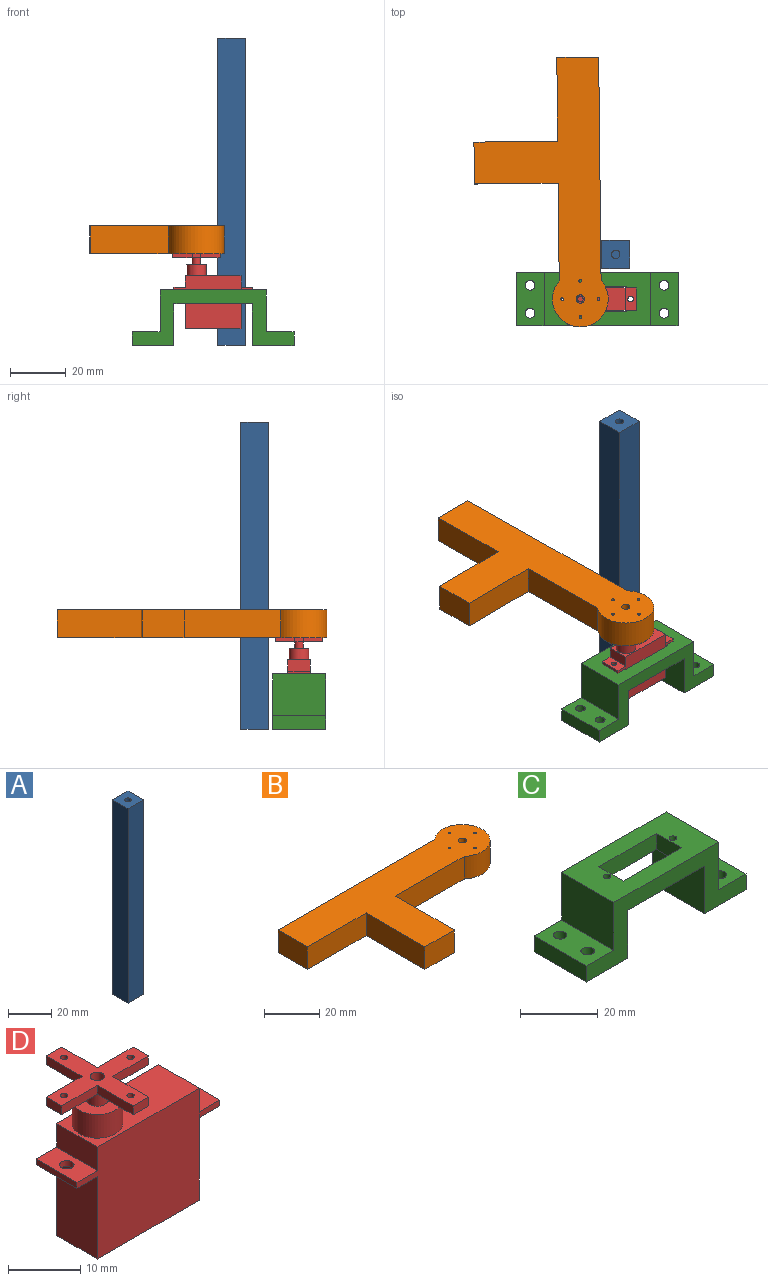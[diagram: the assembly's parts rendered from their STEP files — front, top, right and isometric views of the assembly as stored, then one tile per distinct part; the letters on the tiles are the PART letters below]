
ASSEMBLY  parts=4 mates=2
PART A: 10 faces, bbox 10x10x110 mm
  f0: plane 110x10mm, normal (1,0,0), area 1100mm2, adj f1,f3,f4,f5
  f1: plane 110x10mm, normal (0,1,0), area 1100mm2, adj f0,f2,f4,f5
  f2: plane 110x10mm, normal (-1,0,0), area 1100mm2, adj f1,f3,f4,f5
  f3: plane 110x10mm, normal (0,-1,0), area 1100mm2, adj f0,f2,f4,f5
  f4: plane 10x10mm, normal (0,0,1), area 92.9mm2, adj f0,f1,f2,f3,f8
  f5: plane 10x10mm, normal (0,0,-1), area 92.9mm2, adj f0,f1,f2,f3,f6
  f6: cylinder r=1.5mm len=20mm, axis (0,0,-1), area 188.5mm2, adj f5,f7
  f7: plane 3x3mm, normal (0,0,-1), area 7.1mm2, adj f6
  f8: cylinder r=1.5mm len=30mm, axis (0,0,1), area 282.7mm2, adj f4,f9
  f9: plane 3x3mm, normal (0,0,1), area 7.1mm2, adj f8
PART B: 15 faces, bbox 96.6x47.5x10 mm
  f0: cylinder r=10mm len=20mm, axis (0,0,-1), area 458.7mm2, adj f1,f12,f13,f14
  f1: plane 80x10mm, normal (0,1,0), area 800mm2, adj f0,f2,f13,f14
  f2: plane 15x10mm, normal (-1,0,0), area 150mm2, adj f1,f3,f13,f14
  f3: plane 30x10mm, normal (0,-1,0), area 300mm2, adj f2,f4,f13,f14
  f4: plane 30x10mm, normal (-1,0,0), area 300mm2, adj f3,f5,f13,f14
  f5: plane 15x10mm, normal (0,-1,0), area 150mm2, adj f4,f6,f13,f14
  f6: plane 30x10mm, normal (1,0,0), area 300mm2, adj f5,f12,f13,f14
  f7: cylinder r=1.5mm len=10mm, axis (0,0,-1), area 94.2mm2, adj f13,f14
  f8: cylinder r=0.5mm len=10mm, axis (0,0,-1), area 31.4mm2, adj f13,f14
  f9: cylinder r=0.5mm len=10mm, axis (0,0,-1), area 31.4mm2, adj f13,f14
  f10: cylinder r=0.5mm len=10mm, axis (0,0,-1), area 31.4mm2, adj f13,f14
  f11: cylinder r=0.5mm len=10mm, axis (0,0,-1), area 31.4mm2, adj f13,f14
  f12: plane 35x10mm, normal (0,-1,0), area 350mm2, adj f0,f6,f13,f14
  f13: plane 96.61x47.5mm, normal (0,0,1), area 1918.8mm2, adj f0,f1,f2,f3,f4,f5,f6,f7
  f14: plane 96.61x47.5mm, normal (0,0,-1), area 1918.8mm2, adj f0,f1,f2,f3,f4,f5,f6,f7
PART C: 24 faces, bbox 58x19x20 mm
  f0: plane 28x19mm, normal (0,0,-1), area 336.7mm2, adj f6,f7,f12,f13,f14,f15,f16,f17
  f1: plane 38x19mm, normal (0,0,1), area 526.7mm2, adj f2,f11,f12,f13,f14,f15,f16,f17
  f2: plane 19x15mm, normal (-1,0,0), area 285mm2, adj f1,f3,f12,f13
  f3: plane 19x10mm, normal (0,0,1), area 170.8mm2, adj f2,f4,f12,f13,f22,f23
  f4: plane 19x5mm, normal (-1,0,0), area 95mm2, adj f3,f5,f12,f13
  f5: plane 19x15mm, normal (0,0,-1), area 265.8mm2, adj f4,f6,f12,f13,f22,f23
  f6: plane 19x15mm, normal (1,0,0), area 285mm2, adj f0,f5,f12,f13
  f7: plane 19x15mm, normal (-1,0,0), area 285mm2, adj f0,f8,f12,f13
  f8: plane 19x15mm, normal (0,0,-1), area 265.8mm2, adj f7,f9,f12,f13,f20,f21
  f9: plane 19x5mm, normal (1,0,0), area 95mm2, adj f8,f10,f12,f13
  f10: plane 19x10mm, normal (0,0,1), area 170.8mm2, adj f9,f11,f12,f13,f20,f21
  f11: plane 19x15mm, normal (1,0,0), area 285mm2, adj f1,f10,f12,f13
  f12: plane 58x20mm, normal (0,-1,0), area 440mm2, adj f0,f1,f2,f3,f4,f5,f6,f7
  f13: plane 58x20mm, normal (0,1,0), area 440mm2, adj f0,f1,f2,f3,f4,f5,f6,f7
  f14: plane 9x5mm, normal (-1,0,0), area 45mm2, adj f0,f1,f15,f17
  f15: plane 21x5mm, normal (0,-1,0), area 105mm2, adj f0,f1,f14,f16
  f16: plane 9x5mm, normal (1,0,0), area 45mm2, adj f0,f1,f15,f17
  f17: plane 21x5mm, normal (0,1,0), area 105mm2, adj f0,f1,f14,f16
  f18: cylinder r=1mm len=5mm, axis (0,0,1), area 31.4mm2, adj f0,f1
  f19: cylinder r=1mm len=5mm, axis (0,0,1), area 31.4mm2, adj f0,f1
  f20: cylinder r=1.75mm len=5mm, axis (0,0,1), area 55mm2, adj f8,f10
  f21: cylinder r=1.75mm len=5mm, axis (0,0,1), area 55mm2, adj f8,f10
  f22: cylinder r=1.75mm len=5mm, axis (0,0,1), area 55mm2, adj f3,f5
  f23: cylinder r=1.75mm len=5mm, axis (0,0,1), area 55mm2, adj f3,f5
PART D: 41 faces, bbox 28.5x17x27 mm
  f0: plane 8x4mm, normal (-1,0,0), area 32mm2, adj f3,f5,f6,f16
  f1: plane 14x8mm, normal (1,0,0), area 112mm2, adj f3,f5,f7,f11
  f2: plane 14x8mm, normal (-1,0,0), area 112mm2, adj f3,f5,f7,f15
  f3: plane 24x19mm, normal (0,-1,0), area 384mm2, adj f0,f1,f2,f4,f6,f7,f10,f15
  f4: plane 8x4mm, normal (1,0,0), area 32mm2, adj f3,f5,f6,f13
  f5: plane 24x19mm, normal (0,1,0), area 384mm2, adj f0,f1,f2,f4,f6,f7,f12,f15
  f6: plane 20x8mm, normal (0,0,1), area 121.5mm2, adj f0,f3,f4,f5,f8
  f7: plane 20x8mm, normal (0,0,-1), area 160mm2, adj f1,f2,f3,f5
  f8: cylinder r=3.5mm len=7mm, axis (0,0,-1), area 88mm2, adj f6,f9
  f9: plane 7x7mm, normal (0,0,1), area 31.4mm2, adj f8,f18
  f10: plane 4x1mm, normal (0,-1,0), area 4mm2, adj f3,f11,f13,f14
  f11: plane 8x4mm, normal (0,0,-1), area 28.9mm2, adj f1,f10,f12,f14,f20
  f12: plane 4x1mm, normal (0,1,0), area 4mm2, adj f5,f11,f13,f14
  f13: plane 8x4mm, normal (0,0,1), area 28.9mm2, adj f4,f10,f12,f14,f20
  f14: plane 8x1mm, normal (1,0,0), area 8mm2, adj f10,f11,f12,f13
  f15: plane 8x4mm, normal (0,0,-1), area 28.9mm2, adj f2,f3,f5,f17,f19
  f16: plane 8x4mm, normal (0,0,1), area 28.9mm2, adj f0,f3,f5,f17,f19
  f17: plane 8x1mm, normal (-1,0,0), area 8mm2, adj f3,f5,f15,f16
  f18: cylinder r=1.5mm len=3mm, axis (0,0,-1), area 23.6mm2, adj f9,f34
  f19: cylinder r=1mm len=2mm, axis (0,0,1), area 6.3mm2, adj f15,f16
  f20: cylinder r=1mm len=2mm, axis (0,0,1), area 6.3mm2, adj f11,f13
  f21: plane 7x1.5mm, normal (0,1,0), area 10.5mm2, adj f22,f32,f33,f34
  f22: plane 3x1.5mm, normal (-1,0,0), area 4.5mm2, adj f21,f23,f33,f34
  f23: plane 7x1.5mm, normal (0,-1,0), area 10.5mm2, adj f22,f24,f33,f34
  f24: plane 7x1.5mm, normal (-1,0,0), area 10.5mm2, adj f23,f25,f33,f34
  f25: plane 3x1.5mm, normal (0,-1,0), area 4.5mm2, adj f24,f26,f33,f34
  f26: plane 7x1.5mm, normal (1,0,0), area 10.5mm2, adj f25,f27,f33,f34
  f27: plane 7x1.5mm, normal (0,-1,0), area 10.5mm2, adj f26,f28,f33,f34
  f28: plane 3x1.5mm, normal (1,0,0), area 4.5mm2, adj f27,f29,f33,f34
  f29: plane 7x1.5mm, normal (0,1,0), area 10.5mm2, adj f28,f30,f33,f34
  f30: plane 7x1.5mm, normal (1,0,0), area 10.5mm2, adj f29,f31,f33,f34
  f31: plane 3x1.5mm, normal (0,1,0), area 4.5mm2, adj f30,f32,f33,f34
  f32: plane 7x1.5mm, normal (-1,0,0), area 10.5mm2, adj f21,f31,f33,f34
  f33: plane 17x17mm, normal (0,0,1), area 86.7mm2, adj f21,f22,f23,f24,f25,f26,f27,f28
  f34: plane 17x17mm, normal (0,0,-1), area 82.8mm2, adj f18,f21,f22,f23,f24,f25,f26,f27
  f35: cylinder r=0.5mm len=1.5mm, axis (0,0,1), area 4.7mm2, adj f33,f34
  f36: cylinder r=0.5mm len=1.5mm, axis (0,0,1), area 4.7mm2, adj f33,f34
  f37: cylinder r=0.5mm len=1.5mm, axis (0,0,1), area 4.7mm2, adj f33,f34
  f38: cylinder r=0.5mm len=1.5mm, axis (0,0,1), area 4.7mm2, adj f33,f34
  f39: cylinder r=1mm len=2mm, axis (0,0,1), area 12.6mm2, adj f33,f40
  f40: plane 2x2mm, normal (0,0,1), area 3.1mm2, adj f39
PLACE A t=(6.67,6.38,-17.39)mm
PLACE B rot(axis=(0,0,-1),89.4deg) t=(-6,-9.5,15.5)mm
PLACE C at identity fixed
PLACE D t=(11.75,-3.7,-11.5)mm
MATE revolute B.f7 <-> D.f8  axis (0,0,-1) through (-6,-9.5,15.5)mm
MATE fastened D.f20 <-> C.f18  axis (0,0,-1) through (12,-9.5,2.5)mm
